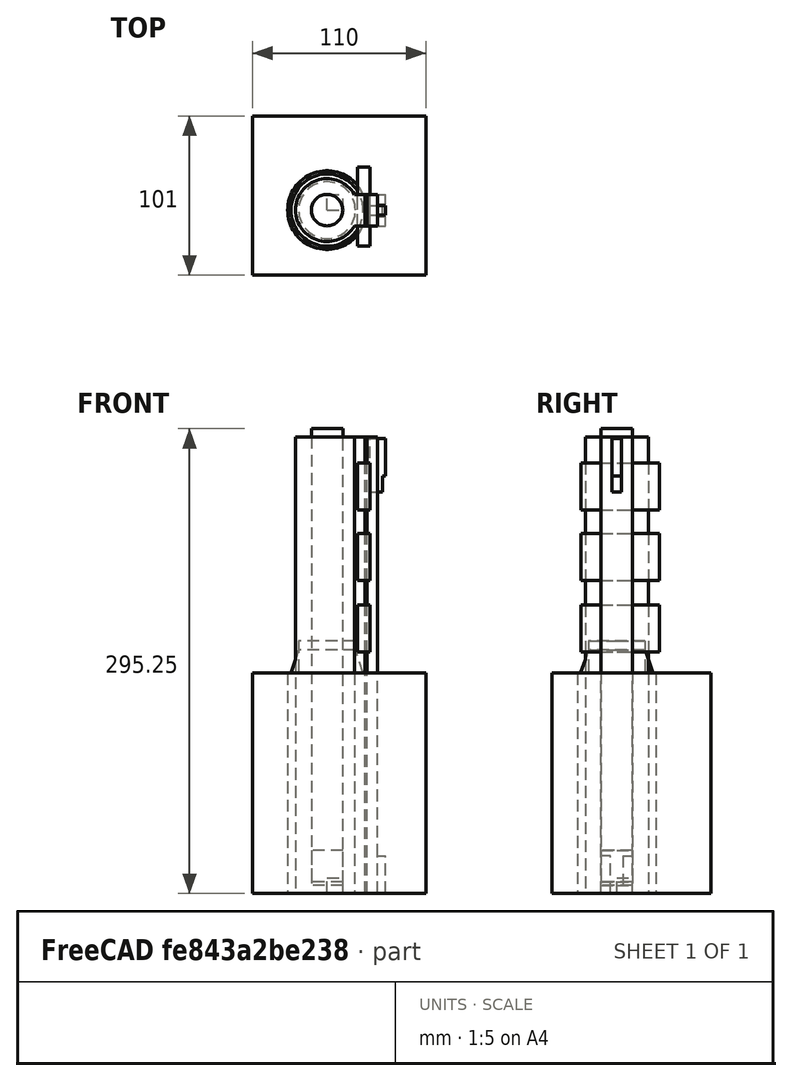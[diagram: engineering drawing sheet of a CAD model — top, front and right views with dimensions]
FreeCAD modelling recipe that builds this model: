
FCSTD DOCUMENT  (FreeCAD 0.20R29410 (Git))
Label: shortBarrel0
License: All rights reserved
LicenseURL: http://en.wikipedia.org/wiki/All_rights_reserved
objects: Part::Box×11, Part::Cylinder×5, Part::MultiFuse×5, Part::Cone×1
note: 22 computed .brp shape members not serialized (recipe doc carries the construction recipe); baked Part::Feature solids carry a one-line shape summary decoded from their .brp

FEATURE [Part::Cylinder] Cylinder
  Angle = 360
  AttacherType = Attacher::AttachEngine3D
  FirstAngle = 0
  Height = 290
  Radius = 20
  SecondAngle = 0
FEATURE [Part::Box] Box  label="Cube"
  AttacherType = Attacher::AttachEngine3D
  Height = 290
  Length = 8
  Placement = pos=(17.25,-10,0) rot=(0,0,1;0rad)
  Width = 20
FEATURE [Part::Cylinder] Cylinder001
  Angle = 360
  AttacherType = Attacher::AttachEngine3D
  FirstAngle = 0
  Height = 140
  Radius = 25
  SecondAngle = 0
FEATURE [Part::Cone] Cone
  Angle = 360
  AttacherType = Attacher::AttachEngine3D
  Height = 15
  Placement = pos=(0,0,139.75) rot=(0,0,1;0rad)
  Radius1 = 23
  Radius2 = 18
FEATURE [Part::Box] Box001  label="Cube001"
  AttacherType = Attacher::AttachEngine3D
  Height = 290
  Length = 8
  Placement = pos=(24,-10,0) rot=(0,0,1;0rad)
  Width = 20
FEATURE [Part::Box] Box002  label="Cube002"
  AttacherType = Attacher::AttachEngine3D
  Height = 24
  Length = 10
  Placement = pos=(27.25,-10,0) rot=(0,0,1;0rad)
  Width = 6
FEATURE [Part::MultiFuse] Fusion  label="MainBarrel"
  Shapes = -> [Cylinder,Box]
FEATURE [Part::MultiFuse] Fusion001  label="RearBarrel"
  Shapes = -> [Cone,Cylinder001]
FEATURE [Part::Box] Box003  label="Cube003"
  AttacherType = Attacher::AttachEngine3D
  Height = 24
  Length = 10
  Placement = pos=(27.25,4,0) rot=(0,0,1;0rad)
  Width = 6
FEATURE [Part::Box] Box004  label="Cube004"
  AttacherType = Attacher::AttachEngine3D
  Height = 24
  Length = 10
  Placement = pos=(27.25,-3,10) rot=(0,0,1;0rad)
  Width = 6
FEATURE [Part::Box] Box005  label="Cube005"
  AttacherType = Attacher::AttachEngine3D
  Height = 34
  Length = 8
  Placement = pos=(27.25,-3,0) rot=(0,0,1;0rad)
  Width = 6
FEATURE [Part::MultiFuse] Fusion002  label="frontSight"
  Placement = pos=(0,0,255) rot=(0,0,1;0rad)
  Shapes = -> [Box004,Box005]
FEATURE [Part::MultiFuse] Fusion003
  Shapes = -> [Box003,Box001]
FEATURE [Part::MultiFuse] Fusion004  label="rearSight"
  Shapes = -> [Fusion003,Box002]
FEATURE [Part::Box] Box006  label="Cube006"
  AttacherType = Attacher::AttachEngine3D
  Height = 30
  Length = 8
  Placement = pos=(19.25,-22.75,153.25) rot=(0,0,1;0rad)
  Width = 50
FEATURE [Part::Box] Box007  label="Cube007"
  AttacherType = Attacher::AttachEngine3D
  Height = 30
  Length = 8
  Placement = pos=(19.25,-22.75,198.75) rot=(0,0,1;0rad)
  Width = 50
FEATURE [Part::Box] Box008  label="Cube008"
  AttacherType = Attacher::AttachEngine3D
  Height = 30
  Length = 8
  Placement = pos=(19.25,-22.75,243.5) rot=(0,0,1;0rad)
  Width = 50
FEATURE [Part::Cylinder] Cylinder002
  Angle = 360
  AttacherType = Attacher::AttachEngine3D
  FirstAngle = 0
  Height = 20
  Placement = pos=(0,0,7.25) rot=(0,0,1;0rad)
  Radius = 10
  SecondAngle = 0
FEATURE [Part::Cylinder] Cylinder003
  Angle = 360
  AttacherType = Attacher::AttachEngine3D
  FirstAngle = 0
  Height = 290
  Placement = pos=(0,0,5.25) rot=(0,0,1;0rad)
  Radius = 10
  SecondAngle = 0
FEATURE [Part::Box] Box009  label="Cube009"
  AttacherType = Attacher::AttachEngine3D
  Height = 10
  Length = 10
  Width = 10
FEATURE [Part::Box] Box010  label="Cube010"
  AttacherType = Attacher::AttachEngine3D
  Height = 140
  Length = 110
  Placement = pos=(-47.25,-41.25,0) rot=(0,0,1;0rad)
  Width = 101
FEATURE [Part::Cylinder] Cylinder004
  Angle = 360
  AttacherType = Attacher::AttachEngine3D
  FirstAngle = 0
  Height = 20
  Placement = pos=(0,0,140.25) rot=(0,0,1;0rad)
  Radius = 18
  SecondAngle = 0
